# Revit family: WH3375-HC-SO
name_source: partatom
category: Plumbing Fixtures
revit_build: Autodesk Revit 2018 (Build: 20170223_1515(x64)
units: mm (PartAtom-declared; Revit-internal decimal feet)

## family parameters
Always vertical = No
Cut with Voids When Loaded = No
OmniClass Number = 23.45.55.14
OmniClass Title = Single Faucets
Part Type = Normal
Room Calculation Point = No
Round Connector Dimension = Use Diameter
Shared = Yes
Work Plane-Based = Yes

## types (1)
- WH3375-HC-SO
    ADA Compliant = Yes
    Assembly Code = D2020
    CW Connection = Yes
    CWFU = 1.5
    Centerset Width = 4"
    Cold Water Connection Diameter = 1"
    Cold Water Connection Radius = 1/2"
    Default Elevation = 0"
    Description = Ligature Resistant Dual Temperature Sensor Activated Faucet - 4 Inch Centerset
    Faucet material = Metal-Whitehalls-Chrome Plated-Cast Bronze
    Flow Rate = 0.5 GPM
    HW Connection = Yes
    HWFU = 1.5
    Hot Water Connection Diameter = 1"
    Hot Water Connection Radius = 1/2"
    Installation Type = Counter Mounted
    Manufacturer = Whitehall Mfg.
    Model = WH3375-HC-SO
    Price = Prices may vary. Please consult Manufacturer Representative for most up-to-date price list.
    Product Documentation Link = https://www.whitehallmfg.com
    Product Page URL = https://www.whitehallmfg.com
    URL = https://www.whitehallmfg.com
    Vent Connection = No
    Voltage = 9 V
    Waste Connection = No

## geometry (parser evidence)
native form markers: Sweep x2
no freeform markers — native parametric forms only
